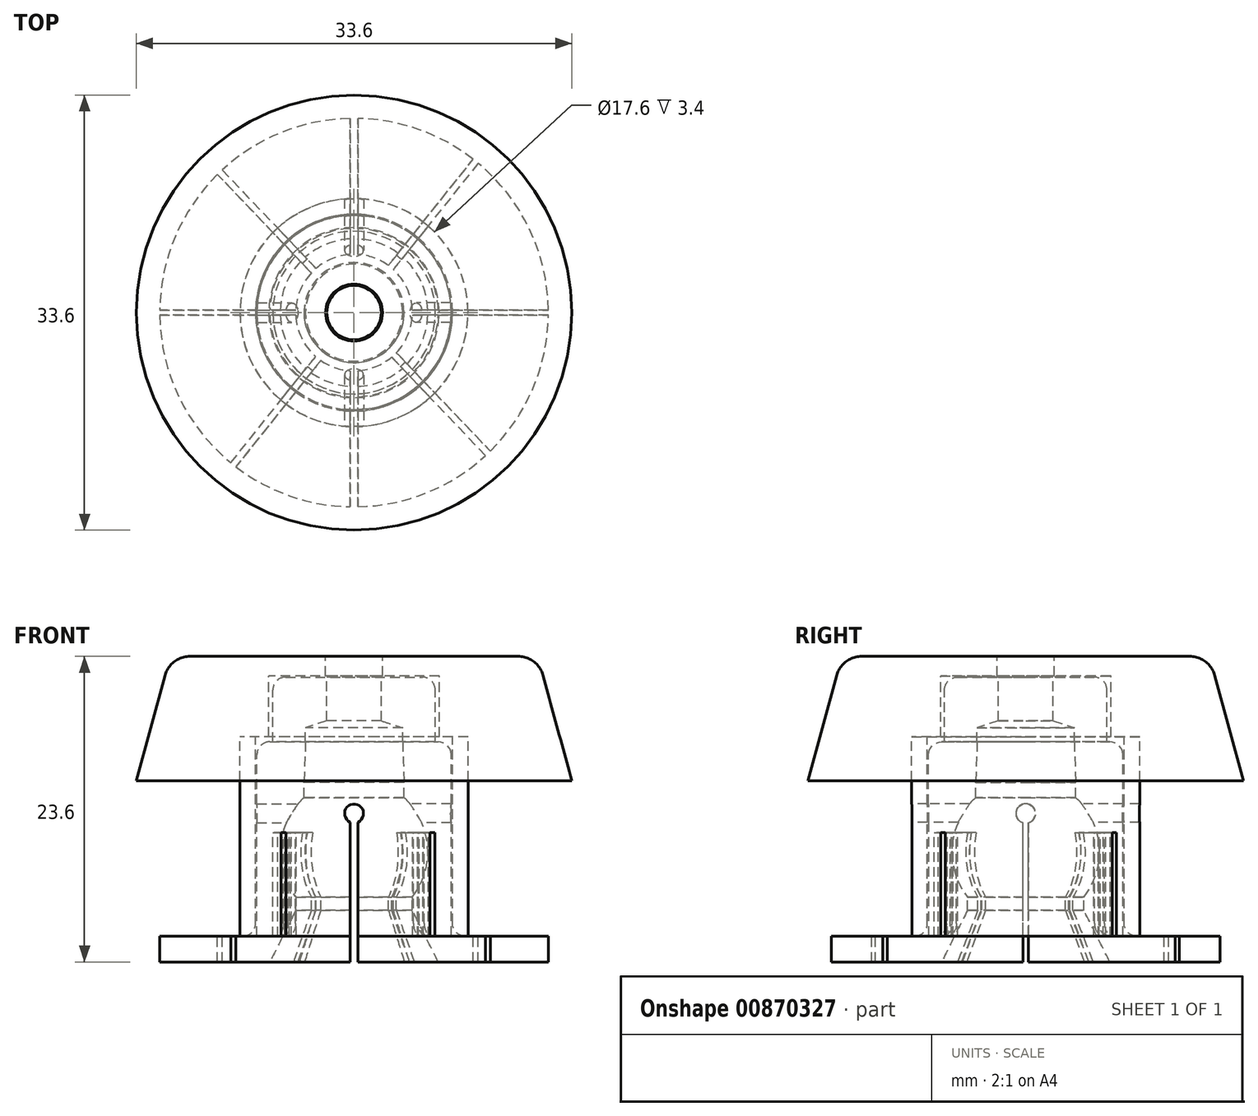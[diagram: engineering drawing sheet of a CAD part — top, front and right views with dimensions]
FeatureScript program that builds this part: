
annotation { "Feature Type Name" : "Feature", "Feature Type Description" : "" }
export const myFeature = defineFeature(function(context is Context, id is Id, definition is map)
    precondition{}
    {
        {
            var Q0;
            Q0=qCreatedBy(makeId("Front.planeOp"),FACE);
            var sketch = newSketch(context, id + "F0", { "sketchPlane" : qUnion([Q0])});
            skLineSegment(sketch, "E0", {"start": v(0, 27.58) * mm, "end": v(0, -29.4) * mm, "construction": true});
            skLineSegment(sketch, "E1", {"start": v(0, 0) * mm, "end": v(-15, 0) * mm});
            skLineSegment(sketch, "E2", {"start": v(-15, 0) * mm, "end": v(-15, 2) * mm});
            skLineSegment(sketch, "E3", {"start": v(-15, 2) * mm, "end": v(-7.5, 2) * mm});
            skLineSegment(sketch, "E4", {"start": v(-7.5, 2) * mm, "end": v(-7.5, 17) * mm});
            skLineSegment(sketch, "E5", {"start": v(-7.5, 17) * mm, "end": v(-6.27, 17) * mm});
            skLineSegment(sketch, "E6", {"start": v(-3.86, 13.85) * mm, "end": v(-3.86, 12.7) * mm});
            skLineSegment(sketch, "E7", {"start": v(-4.5, 0) * mm, "end": v(-4.5, 5) * mm});
            skArc(sketch, "E8", {"start": v(-3.86, 12.7) * mm, "mid": v(-5.68, 8.97) * mm, "end": v(-4.5, 5) * mm});
            skLineSegment(sketch, "E9", {"start": v(-6.27, 17) * mm, "end": v(-6.27, 22) * mm});
            skLineSegment(sketch, "E10", {"start": v(-6.27, 22) * mm, "end": v(-2.1, 22) * mm});
            skLineSegment(sketch, "E11", {"start": v(-2.1, 22) * mm, "end": v(-2.1, 18.62) * mm});
            skLineSegment(sketch, "E12", {"start": v(-2.1, 18.62) * mm, "end": v(-3.75, 18.09) * mm});
            skLineSegment(sketch, "E13", {"start": v(-3.75, 18.09) * mm, "end": v(-3.75, 17) * mm});
            skLineSegment(sketch, "E14", {"start": v(-3.75, 17) * mm, "end": v(-3.86, 13.85) * mm});
            skSolve(sketch);
        }
        {
            var Q0;
            {var subQ1=sQuery(id+"F0.wireOp",EDGE,"E2");Q0=makeQuery(id+"F0.imprint","IMPRINT",FACE,{"disambiguationData":[TD([[makeQuery(id+"F0.imprint","IMPRINT",EDGE,{"derivedFrom":subQ1}),-1.0]])]});}
            var Q1;
            Q1=sQuery(id+"F0.wireOp",EDGE,"E0");
            revolve(context, id + "F1", {"surfaceOperationType" : NewSurfaceOperationType.NEW, "entities" : qUnion([Q0]), "axis" : qUnion([Q1]), "revolveType" : RevolveType.FULL});
        }
        {
            var Q0;
            Q0=makeQuery(id+"F1.opRevolve","SWEPT_EDGE",EDGE,{"disambiguationData":[OSD([sQuery(id+"F0.wireOp",EDGE,"E1"),sQuery(id+"F0.wireOp",EDGE,"E7")])]});
            chamfer(context, id + "F2", {"entities" : qUnion([Q0]), "chamferType" : ChamferType.TWO_OFFSETS, "width1" : 2 * mm, "oppositeDirection" : false, "width2" : 4 * mm, "tangentPropagation" : true});
        }
        {
            var Q0;
            Q0=qCreatedBy(makeId("Front.planeOp"),FACE);
            var sketch = newSketch(context, id + "F3", { "sketchPlane" : qUnion([Q0])});
            skLineSegment(sketch, "E15.bottom", {"start": v(18.23, -4.17) * mm, "end": v(-16.48, -4.17) * mm});
            skLineSegment(sketch, "E15.top", {"start": v(18.23, 11.5) * mm, "end": v(-16.48, 11.5) * mm});
            skLineSegment(sketch, "E15.left", {"start": v(18.23, -4.17) * mm, "end": v(18.23, 11.5) * mm});
            skLineSegment(sketch, "E15.right", {"start": v(-16.48, -4.17) * mm, "end": v(-16.48, 11.5) * mm});
            skSolve(sketch);
        }
        {
            var Q0;
            Q0=makeQuery(id+"F3.imprint","IMPRINT",FACE,{"disambiguationData":[TD([[makeQuery(id+"F3.imprint","IMPRINT",EDGE,{"derivedFrom":sQuery(id+"F3.wireOp",EDGE,"E15.bottom")}),-1.0]])]});
            extrude(context, id + "F4", {"entities" : qUnion([Q0]), "operationType" : NewBodyOperationType.REMOVE, "depth" : .2 * mm, "offsetDistance" : 25 * mm, "hasSecondDirection" : true, "secondDirectionOppositeDirection" : true, "secondDirectionDepth" : .2 * mm});
        }
        {
            var Q0;
            Q0=makeQuery(id+"F1.opRevolve","SWEPT_EDGE",EDGE,{"disambiguationData":[OSD([sQuery(id+"F0.wireOp",EDGE,"E4"),sQuery(id+"F0.wireOp",EDGE,"E5")])]});
            var Q1;
            Q1=makeQuery(id+"F1.opRevolve","SWEPT_EDGE",EDGE,{"disambiguationData":[OSD([sQuery(id+"F0.wireOp",EDGE,"E9"),sQuery(id+"F0.wireOp",EDGE,"E10")])]});
            fillet(context, id + "F5", {"entities" : qUnion([Q0, Q1]), "radius" : 1 * mm, "tangentPropagation" : true, "allowEdgeOverflow" : false});
        }
        {
            var Q0;
            Q0=qCreatedBy(makeId("Front.planeOp"),FACE);
            var sketch = newSketch(context, id + "F6", { "sketchPlane" : qUnion([Q0])});
            skLineSegment(sketch, "E16", {"start": v(-16.8, 14) * mm, "end": v(-8.8, 14) * mm});
            skLineSegment(sketch, "E17", {"start": v(-8.8, 14) * mm, "end": v(-8.8, 17.4) * mm});
            skLineSegment(sketch, "E18", {"start": v(-8.8, 17.4) * mm, "end": v(-6.57, 17.4) * mm});
            skLineSegment(sketch, "E19", {"start": v(-6.57, 17.4) * mm, "end": v(-6.57, 22.1) * mm});
            skLineSegment(sketch, "E20", {"start": v(-6.57, 22.1) * mm, "end": v(-2.2, 22.1) * mm});
            skLineSegment(sketch, "E21", {"start": v(-2.2, 22.1) * mm, "end": v(-2.2, 23.6) * mm});
            skLineSegment(sketch, "E22", {"start": v(-2.2, 23.6) * mm, "end": v(-14.2, 23.6) * mm});
            skLineSegment(sketch, "E23", {"start": v(-14.2, 23.6) * mm, "end": v(-16.8, 14) * mm});
            skLineSegment(sketch, "E24", {"start": v(-7.6, -1.8) * mm, "end": v(-7.6, 13.18) * mm, "construction": true});
            skLineSegment(sketch, "E25", {"start": v(-7.6, 2.02) * mm, "end": v(-7.6, 17.4) * mm});
            skPoint(sketch, "E25.endSnap0", {"position": v(-7.69, 17.4) * mm});
            skLineSegment(sketch, "E26", {"start": v(-7.6, 17.4) * mm, "end": v(-8.8, 17.4) * mm});
            skLineSegment(sketch, "E27", {"start": v(-8.8, 17.4) * mm, "end": v(-8.8, 1.98) * mm});
            skLineSegment(sketch, "E28", {"start": v(-8.8, 1.98) * mm, "end": v(-7.6, 2.02) * mm});
            skSolve(sketch);
        }
        {
            var Q0;
            Q0=makeQuery(id+"F6.imprint","IMPRINT",FACE,{"disambiguationData":[TD([[makeQuery(id+"F6.imprint","IMPRINT",EDGE,{"derivedFrom":sQuery(id+"F6.wireOp",EDGE,"E16")}),1.0]])]});
            var Q1;
            {var subQ0=sQuery(id+"F6.wireOp",EDGE,"E18");Q1=makeQuery(id+"F6.imprint","IMPRINT",FACE,{"disambiguationData":[TD([[makeQuery(id+"F6.imprint","IMPRINT",EDGE,{"derivedFrom":subQ0}),1.0]])]});}
            var Q2;
            {var subQ1=sQuery(id+"F6.wireOp",EDGE,"E17");Q2=makeQuery(id+"F6.imprint","IMPRINT",FACE,{"disambiguationData":[TD([[makeQuery(id+"F6.imprint","IMPRINT",EDGE,{"derivedFrom":subQ1}),-1.0]])]});}
            var Q3;
            Q3=makeQuery(id+"F6.imprint","IMPRINT",FACE,{"disambiguationData":[TD([[makeQuery(id+"F6.imprint","IMPRINT",EDGE,{"derivedFrom":sQuery(id+"F6.wireOp",EDGE,"E25")}),1.0]])]});
            var Q4;
            Q4=sQuery(id+"F0.wireOp",EDGE,"E0");
            revolve(context, id + "F7", {"surfaceOperationType" : NewSurfaceOperationType.NEW, "entities" : qUnion([Q0, Q1, Q2, Q3]), "axis" : qUnion([Q4]), "revolveType" : RevolveType.FULL});
        }
        {
            var Q0;
            Q0=makeQuery(id+"F7.opRevolve","SWEPT_EDGE",EDGE,{"disambiguationData":[OSD([sQuery(id+"F6.wireOp",EDGE,"E22"),sQuery(id+"F6.wireOp",EDGE,"E23")])]});
            fillet(context, id + "F8", {"entities" : qUnion([Q0]), "radius" : 2 * mm, "tangentPropagation" : true, "allowEdgeOverflow" : false});
        }
        {
            var Q0;
            Q0=qCreatedBy(makeId("Right.planeOp"),FACE);
            var sketch = newSketch(context, id + "F9", { "sketchPlane" : qUnion([Q0])});
            skPoint(sketch, "E29", {"position": v(0, 11.47) * mm});
            skSolve(sketch);
        }
        {
            var Q0;
            Q0=sQuery(id+"F9.wireOp",VERTEX,"E29");
            var Q1;
            Q1=makeQuery(id+"F1.opRevolve","SWEPT_BODY",BODY,{"disambiguationData":[OSD([sQuery(id+"F0.wireOp",EDGE,"E1"),sQuery(id+"F0.wireOp",EDGE,"E2"),sQuery(id+"F0.wireOp",EDGE,"E3"),sQuery(id+"F0.wireOp",EDGE,"E4"),sQuery(id+"F0.wireOp",EDGE,"E5"),sQuery(id+"F0.wireOp",EDGE,"E6"),sQuery(id+"F0.wireOp",EDGE,"E7"),sQuery(id+"F0.wireOp",EDGE,"E8"),sQuery(id+"F0.wireOp",EDGE,"E9"),sQuery(id+"F0.wireOp",EDGE,"E10"),sQuery(id+"F0.wireOp",EDGE,"E11"),sQuery(id+"F0.wireOp",EDGE,"E12"),sQuery(id+"F0.wireOp",EDGE,"E13"),sQuery(id+"F0.wireOp",EDGE,"E14")])]});
            hole(context, id + "F10", {"style" : HoleStyle.SIMPLE, "endStyle" : HoleEndStyle.THROUGH, "holeDiameter" : 1.5 * mm, "majorDiameter" : 5 * mm, "isTappedThrough" : true, "tappedDepth" : 12 * mm, "tapClearance" : 3, "locations" : qUnion([Q0]), "scope" : qUnion([Q1])});
        }
        {
            var Q0;
            Q0=sQuery(id+"F9.wireOp",VERTEX,"E29");
            var Q1;
            Q1=makeQuery(id+"F1.opRevolve","SWEPT_BODY",BODY,{"disambiguationData":[OSD([sQuery(id+"F0.wireOp",EDGE,"E1"),sQuery(id+"F0.wireOp",EDGE,"E2"),sQuery(id+"F0.wireOp",EDGE,"E3"),sQuery(id+"F0.wireOp",EDGE,"E4"),sQuery(id+"F0.wireOp",EDGE,"E5"),sQuery(id+"F0.wireOp",EDGE,"E6"),sQuery(id+"F0.wireOp",EDGE,"E7"),sQuery(id+"F0.wireOp",EDGE,"E8"),sQuery(id+"F0.wireOp",EDGE,"E9"),sQuery(id+"F0.wireOp",EDGE,"E10"),sQuery(id+"F0.wireOp",EDGE,"E11"),sQuery(id+"F0.wireOp",EDGE,"E12"),sQuery(id+"F0.wireOp",EDGE,"E13"),sQuery(id+"F0.wireOp",EDGE,"E14")])]});
            hole(context, id + "F11", {"style" : HoleStyle.SIMPLE, "endStyle" : HoleEndStyle.THROUGH, "oppositeDirection" : true, "holeDiameter" : 1.5 * mm, "majorDiameter" : 5 * mm, "isTappedThrough" : true, "tappedDepth" : 12 * mm, "tapClearance" : 3, "locations" : qUnion([Q0]), "scope" : qUnion([Q1])});
        }
        {
            var Q0;
            Q0=qCreatedBy(makeId("Right.planeOp"),FACE);
            var sketch = newSketch(context, id + "F12", { "sketchPlane" : qUnion([Q0])});
            skLineSegment(sketch, "E30.bottom", {"start": v(22.15, 11.5) * mm, "end": v(-24.54, 11.5) * mm});
            skLineSegment(sketch, "E30.top", {"start": v(22.15, -10.49) * mm, "end": v(-24.54, -10.49) * mm});
            skLineSegment(sketch, "E30.left", {"start": v(22.15, 11.5) * mm, "end": v(22.15, -10.49) * mm});
            skLineSegment(sketch, "E30.right", {"start": v(-24.54, 11.5) * mm, "end": v(-24.54, -10.49) * mm});
            skSolve(sketch);
        }
        {
            var Q0;
            Q0=makeQuery(id+"F12.imprint","IMPRINT",FACE,{"disambiguationData":[TD([[makeQuery(id+"F12.imprint","IMPRINT",EDGE,{"derivedFrom":sQuery(id+"F12.wireOp",EDGE,"E30.bottom")}),1.0]])]});
            extrude(context, id + "F13", {"entities" : qUnion([Q0]), "operationType" : NewBodyOperationType.REMOVE, "depth" : .3 * mm, "offsetDistance" : 25 * mm, "hasSecondDirection" : true, "secondDirectionOppositeDirection" : true, "secondDirectionDepth" : .3 * mm});
        }
        {
            var Q0;
            Q0=makeQuery(id+"F7.opRevolve","SWEPT_EDGE",EDGE,{"disambiguationData":[OSD([sQuery(id+"F6.wireOp",EDGE,"E25"),sQuery(id+"F6.wireOp",EDGE,"E28")])]});
            fillet(context, id + "F14", {"entities" : qUnion([Q0]), "radius" : 1 * mm, "tangentPropagation" : true, "allowEdgeOverflow" : false});
        }
        {
            var Q0;
            Q0=qCreatedBy(makeId("Front.planeOp"),FACE);
            var sketch = newSketch(context, id + "F15", { "sketchPlane" : qUnion([Q0])});
            skCircle(sketch, "E31", {"center": v(0, 11.46) * mm, "radius": 0.73 * mm});
            skSolve(sketch);
        }
        {
            var Q0;
            Q0=makeQuery(id+"F15.imprint","IMPRINT",FACE,{"disambiguationData":[TD([[makeQuery(id+"F15.imprint","IMPRINT",EDGE,{"derivedFrom":sQuery(id+"F15.wireOp",EDGE,"E31")}),1.0]])]});
            extrude(context, id + "F16", {"entities" : qUnion([Q0]), "operationType" : NewBodyOperationType.REMOVE, "oppositeDirection" : true, "depth" : 25 * mm, "offsetDistance" : 25 * mm, "hasSecondDirection" : true, "secondDirectionOppositeDirection" : false, "secondDirectionDepth" : 25 * mm});
        }
        {
            var Q0;
            {var subQ1=sQuery(id+"F0.wireOp",EDGE,"E1");var subQ3=makeQuery(id+"F4.opExtrude","CAP_FACE",FACE,{"disambiguationData":[OSD([sQuery(id+"F3.wireOp",EDGE,"E15.bottom"),sQuery(id+"F3.wireOp",EDGE,"E15.top"),sQuery(id+"F3.wireOp",EDGE,"E15.left"),sQuery(id+"F3.wireOp",EDGE,"E15.right")])],"isStart":false});Q0=makeQuery(id+"F13.boolean.opBoolean","SPLIT",FACE,{"disambiguationData":[TD([makeQuery(id+"F4.boolean.opBoolean","COPY",FACE,{"disambiguationData":[OD(1.0)],"derivedFrom":subQ3})])],"derivedFrom":makeQuery(id+"F4.boolean.opBoolean","SPLIT",FACE,{"disambiguationData":[TD([subQ3])],"derivedFrom":makeQuery(id+"F1.opRevolve","SWEPT_FACE",FACE,{"disambiguationData":[OSD([subQ1])]})})});}
            var sketch = newSketch(context, id + "F17", { "sketchPlane" : qUnion([Q0])});
            skLineSegment(sketch, "E32", {"start": v(10.76, 11.69) * mm, "end": v(-23.73, -24.51) * mm});
            skLineSegment(sketch, "E33", {"start": v(-23.73, -24.51) * mm, "end": v(-23.36, -24.86) * mm});
            skLineSegment(sketch, "E34", {"start": v(-23.36, -24.86) * mm, "end": v(11.21, 11.43) * mm});
            skLineSegment(sketch, "E35", {"start": v(11.21, 11.43) * mm, "end": v(10.76, 11.69) * mm});
            skLineSegment(sketch, "E36", {"start": v(-11.41, 14.77) * mm, "end": v(-11.78, 14.43) * mm});
            skLineSegment(sketch, "E37", {"start": v(-11.78, 14.43) * mm, "end": v(9.68, -12.45) * mm});
            skLineSegment(sketch, "E38", {"start": v(9.68, -12.45) * mm, "end": v(10.03, -12.09) * mm});
            skLineSegment(sketch, "E39", {"start": v(10.03, -12.09) * mm, "end": v(-11.41, 14.77) * mm});
            skSolve(sketch);
        }
        {
            var Q0;
            {var subQ5=sQuery(id+"F17.wireOp",EDGE,"E36");Q0=makeQuery(id+"F17.imprint","IMPRINT",FACE,{"disambiguationData":[TD([[makeQuery(id+"F17.imprint","IMPRINT",EDGE,{"derivedFrom":subQ5}),1.0]])]});}
            var Q1;
            {var subQ0=sQuery(id+"F17.wireOp",EDGE,"E33");Q1=makeQuery(id+"F17.imprint","IMPRINT",FACE,{"disambiguationData":[TD([[makeQuery(id+"F17.imprint","IMPRINT",EDGE,{"derivedFrom":subQ0}),1.0]])]});}
            var Q2;
            {var subQ5=sQuery(id+"F17.wireOp",EDGE,"E38");Q2=makeQuery(id+"F17.imprint","IMPRINT",FACE,{"disambiguationData":[TD([[makeQuery(id+"F17.imprint","IMPRINT",EDGE,{"derivedFrom":subQ5}),1.0]])]});}
            var Q3;
            {var subQ0=sQuery(id+"F17.wireOp",EDGE,"E39");var subQ1=sQuery(id+"F17.wireOp",EDGE,"E32");var subQ2=makeQuery(id+"F17.imprint","INTERSECT",VERTEX,{"derivedFrom":[subQ1,subQ0]});Q3=makeQuery(id+"F17.imprint","IMPRINT",FACE,{"disambiguationData":[TD([[makeQuery(id+"F17.imprint","IMPRINT",EDGE,{"disambiguationData":[TD([[subQ2,1.0]])],"derivedFrom":subQ0}),-1.0]])]});}
            var Q4;
            {var subQ0=sQuery(id+"F17.wireOp",EDGE,"E32");var subQ1=sQuery(id+"F0.wireOp",EDGE,"E1");var subQ3=makeQuery(id+"F4.opExtrude","CAP_FACE",FACE,{"disambiguationData":[OSD([sQuery(id+"F3.wireOp",EDGE,"E15.bottom"),sQuery(id+"F3.wireOp",EDGE,"E15.top"),sQuery(id+"F3.wireOp",EDGE,"E15.left"),sQuery(id+"F3.wireOp",EDGE,"E15.right")])],"isStart":false});var subQ4=makeQuery(id+"F4.boolean.opBoolean","COPY",FACE,{"disambiguationData":[OD(1.0)],"derivedFrom":subQ3});var subQ6=sQuery(id+"F0.wireOp",EDGE,"E2");var subQ8=makeQuery(id+"F13.boolean.opBoolean","SPLIT",EDGE,{"disambiguationData":[TD([subQ4])],"derivedFrom":makeQuery(id+"F4.boolean.opBoolean","SPLIT",EDGE,{"disambiguationData":[TD([subQ3])],"derivedFrom":makeQuery(id+"F1.opRevolve","SWEPT_EDGE",EDGE,{"disambiguationData":[OSD([subQ1,subQ6])]})})});var subQ9=makeQuery(id+"F17.imprint","INTERSECT",VERTEX,{"derivedFrom":[subQ8,subQ0]});Q4=makeQuery(id+"F17.imprint","IMPRINT",FACE,{"disambiguationData":[TD([[makeQuery(id+"F17.imprint","IMPRINT",EDGE,{"disambiguationData":[TD([[subQ9,-1.0]])],"derivedFrom":subQ0}),1.0]])]});}
            extrude(context, id + "F18", {"entities" : qUnion([Q0, Q1, Q2, Q3, Q4]), "operationType" : NewBodyOperationType.REMOVE, "oppositeDirection" : true, "depth" : 10 * mm, "offsetDistance" : 25 * mm});
        }
    });
